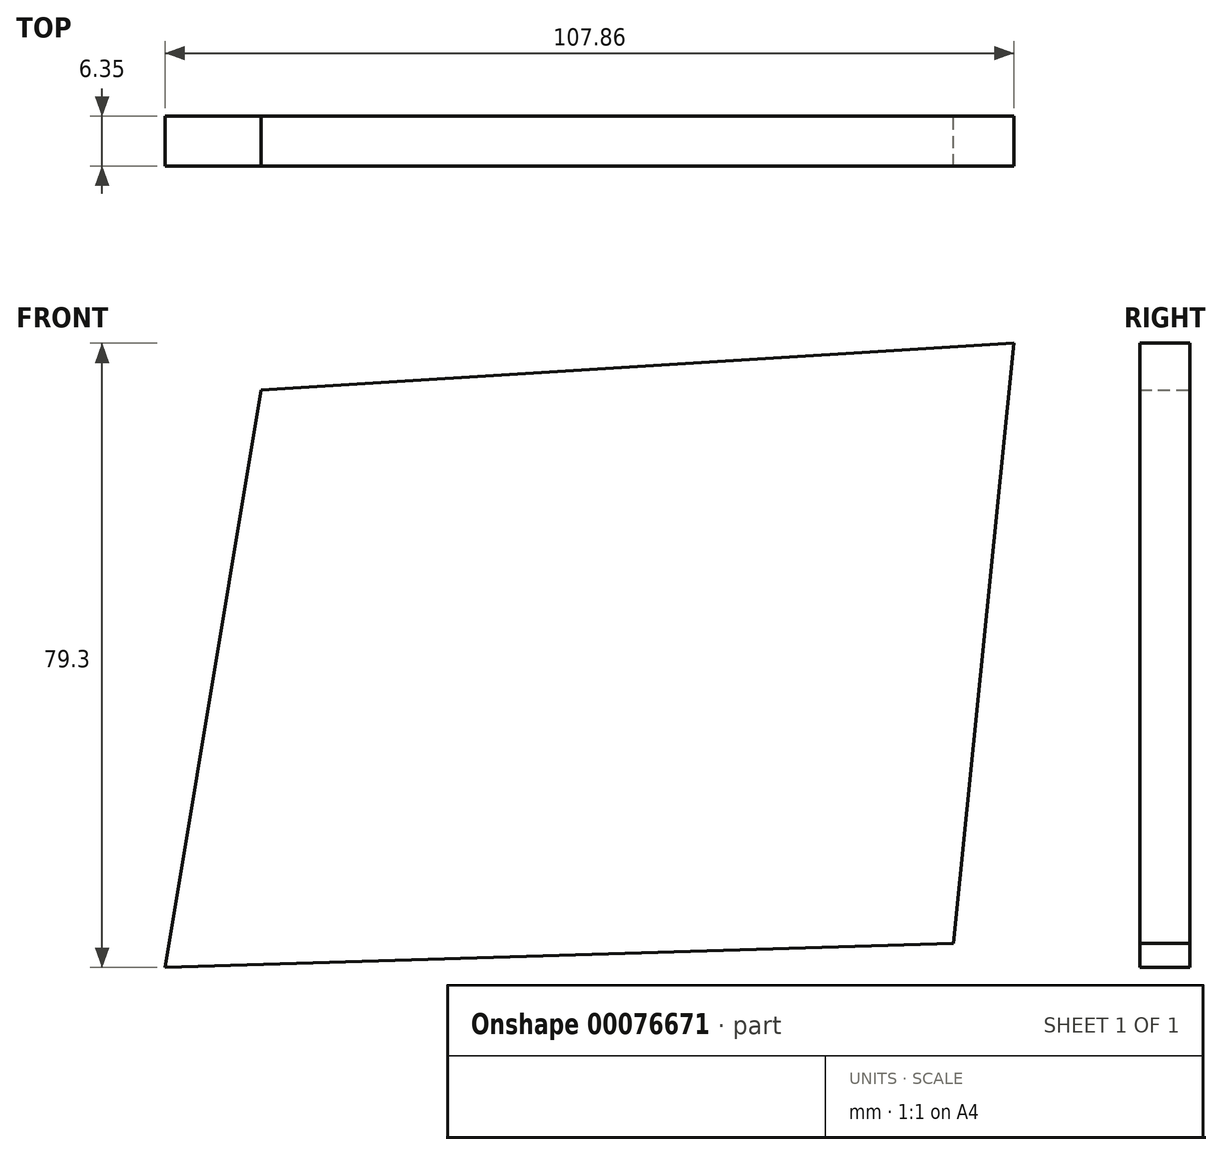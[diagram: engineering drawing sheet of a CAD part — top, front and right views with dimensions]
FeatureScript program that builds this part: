
annotation { "Feature Type Name" : "Feature", "Feature Type Description" : "" }
export const myFeature = defineFeature(function(context is Context, id is Id, definition is map)
    precondition{}
    {
        {
            var Q0;
            Q0=qCreatedBy(makeId("Front.planeOp"),FACE);
            var sketch = newSketch(context, id + "F0", { "sketchPlane" : qUnion([Q0])});
            skLineSegment(sketch, "E0", {"start": v(-92.85, 3.91) * mm, "end": v(-105.07, -69.42) * mm});
            skLineSegment(sketch, "E1", {"start": v(2.8, 9.88) * mm, "end": v(-4.89, -66.33) * mm});
            skLineSegment(sketch, "E2", {"start": v(-105.07, -69.42) * mm, "end": v(-4.89, -66.33) * mm});
            skLineSegment(sketch, "E3", {"start": v(-92.85, 3.91) * mm, "end": v(2.8, 9.88) * mm});
            skSolve(sketch);
        }
        {
            var Q0;
            Q0=makeQuery(id+"F0.imprint","IMPRINT",FACE,{"disambiguationData":[TD([[makeQuery(id+"F0.imprint","IMPRINT",EDGE,{"derivedFrom":sQuery(id+"F0.wireOp",EDGE,"E0")}),1.0]])]});
            extrude(context, id + "F1", {"entities" : qUnion([Q0]), "depth" : 6.35 * mm});
        }
    });
